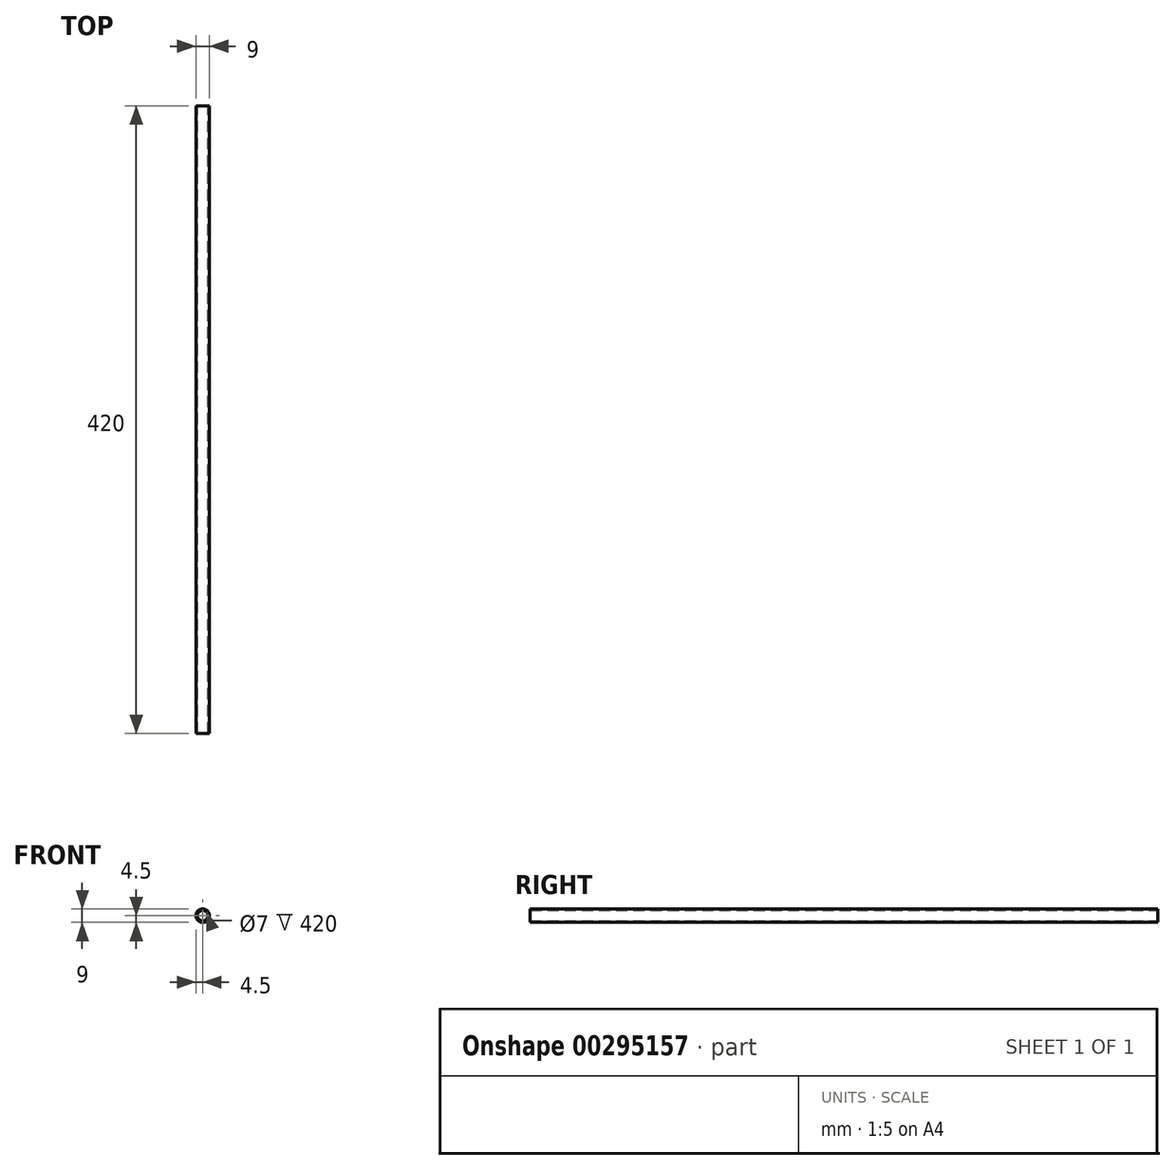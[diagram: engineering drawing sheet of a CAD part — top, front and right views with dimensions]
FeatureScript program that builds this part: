
annotation { "Feature Type Name" : "Feature", "Feature Type Description" : "" }
export const myFeature = defineFeature(function(context is Context, id is Id, definition is map)
    precondition{}
    {
        {
            var Q0;
            Q0=qCreatedBy(makeId("Front.planeOp"),FACE);
            var sketch = newSketch(context, id + "F0", { "sketchPlane" : qUnion([Q0])});
            skCircle(sketch, "E0", {"center": v(0, 0) * mm, "radius": 4.5 * mm});
            skSolve(sketch);
        }
        {
            var Q0;
            Q0=makeQuery(id+"F0.imprint","IMPRINT",FACE,{"disambiguationData":[TD([[makeQuery(id+"F0.imprint","IMPRINT",EDGE,{"derivedFrom":sQuery(id+"F0.wireOp",EDGE,"E0")}),1.0]])]});
            extrude(context, id + "F1", {"entities" : qUnion([Q0]), "endBound" : BoundingType.SYMMETRIC, "depth" : 420 * mm});
        }
        {
            var Q0;
            Q0=makeQuery(id+"F1.opExtrude","CAP_FACE",FACE,{"disambiguationData":[OSD([sQuery(id+"F0.wireOp",EDGE,"E0")])],"isStart":false});
            var Q1;
            Q1=makeQuery(id+"F1.opExtrude","CAP_FACE",FACE,{"disambiguationData":[OSD([sQuery(id+"F0.wireOp",EDGE,"E0")])],"isStart":true});
            shell(context, id + "F2", {"entities" : qUnion([Q0, Q1]), "thickness" : 1 * mm});
        }
    });
